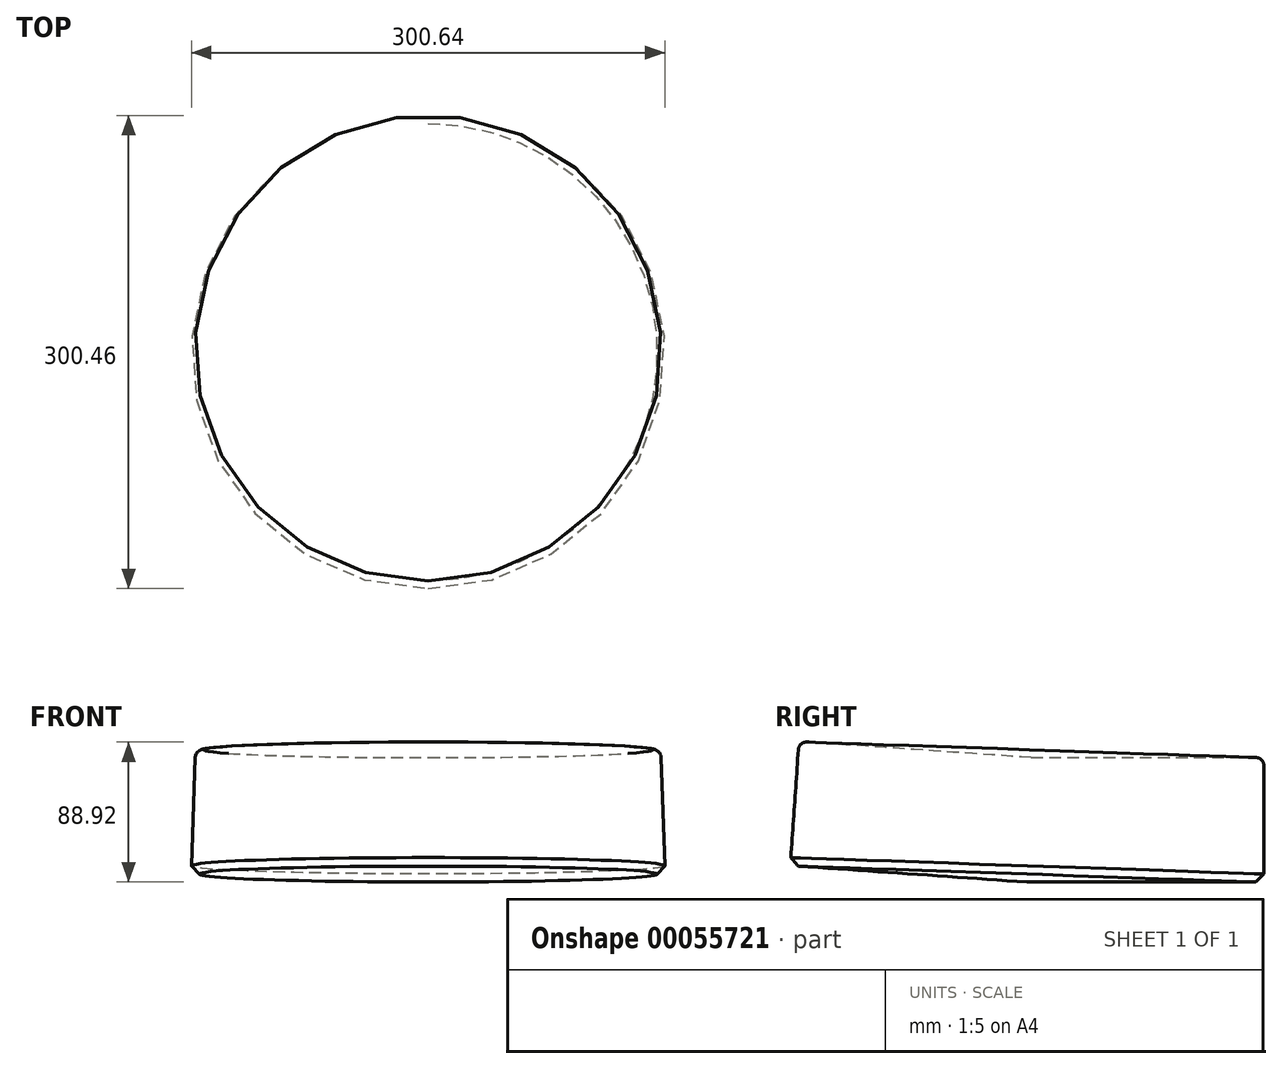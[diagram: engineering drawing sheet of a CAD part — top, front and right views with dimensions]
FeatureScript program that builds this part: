
annotation { "Feature Type Name" : "Feature", "Feature Type Description" : "" }
export const myFeature = defineFeature(function(context is Context, id is Id, definition is map)
    precondition{}
    {
        {
            var Q0;
            Q0=qCreatedBy(makeId("Right.planeOp"),FACE);
            var sketch = newSketch(context, id + "F0", { "sketchPlane" : qUnion([Q0])});
            skLineSegment(sketch, "E0", {"start": v(-74.58, 0) * mm, "end": v(76, 0) * mm});
            skLineSegment(sketch, "E1", {"start": v(76, 0) * mm, "end": v(76, 79.02) * mm});
            skLineSegment(sketch, "E2", {"start": v(76, 79.02) * mm, "end": v(-71.84, 79.02) * mm});
            skLineSegment(sketch, "E3", {"start": v(-71.84, 79.02) * mm, "end": v(-74.58, 0) * mm});
            skSolve(sketch);
        }
        {
            var Q0;
            Q0 = qSketchRegion(id + "F0", true);
            var Q1;
            Q1=sQuery(id+"F0.wireOp",EDGE,"E3");
            revolve(context, id + "F1", {"entities" : qUnion([Q0]), "axis" : qUnion([Q1]), "revolveType" : RevolveType.FULL});
        }
        {
            var Q0;
            Q0=makeQuery(id+"F1.opRevolve","SWEPT_EDGE",EDGE,{"disambiguationData":[OSD([sQuery(id+"F0.wireOp",EDGE,"E1"),sQuery(id+"F0.wireOp",EDGE,"E2")])]});
            fillet(context, id + "F2", {"entities" : qUnion([Q0]), "radius" : 5.08 * mm, "tangentPropagation" : true, "allowEdgeOverflow" : false});
        }
        {
            var Q0;
            Q0=makeQuery(id+"F1.opRevolve","SWEPT_EDGE",EDGE,{"disambiguationData":[OSD([sQuery(id+"F0.wireOp",EDGE,"E0"),sQuery(id+"F0.wireOp",EDGE,"E1")])]});
            chamfer(context, id + "F3", {"entities" : qUnion([Q0]), "width" : 5.08 * mm, "tangentPropagation" : true});
        }
    });
